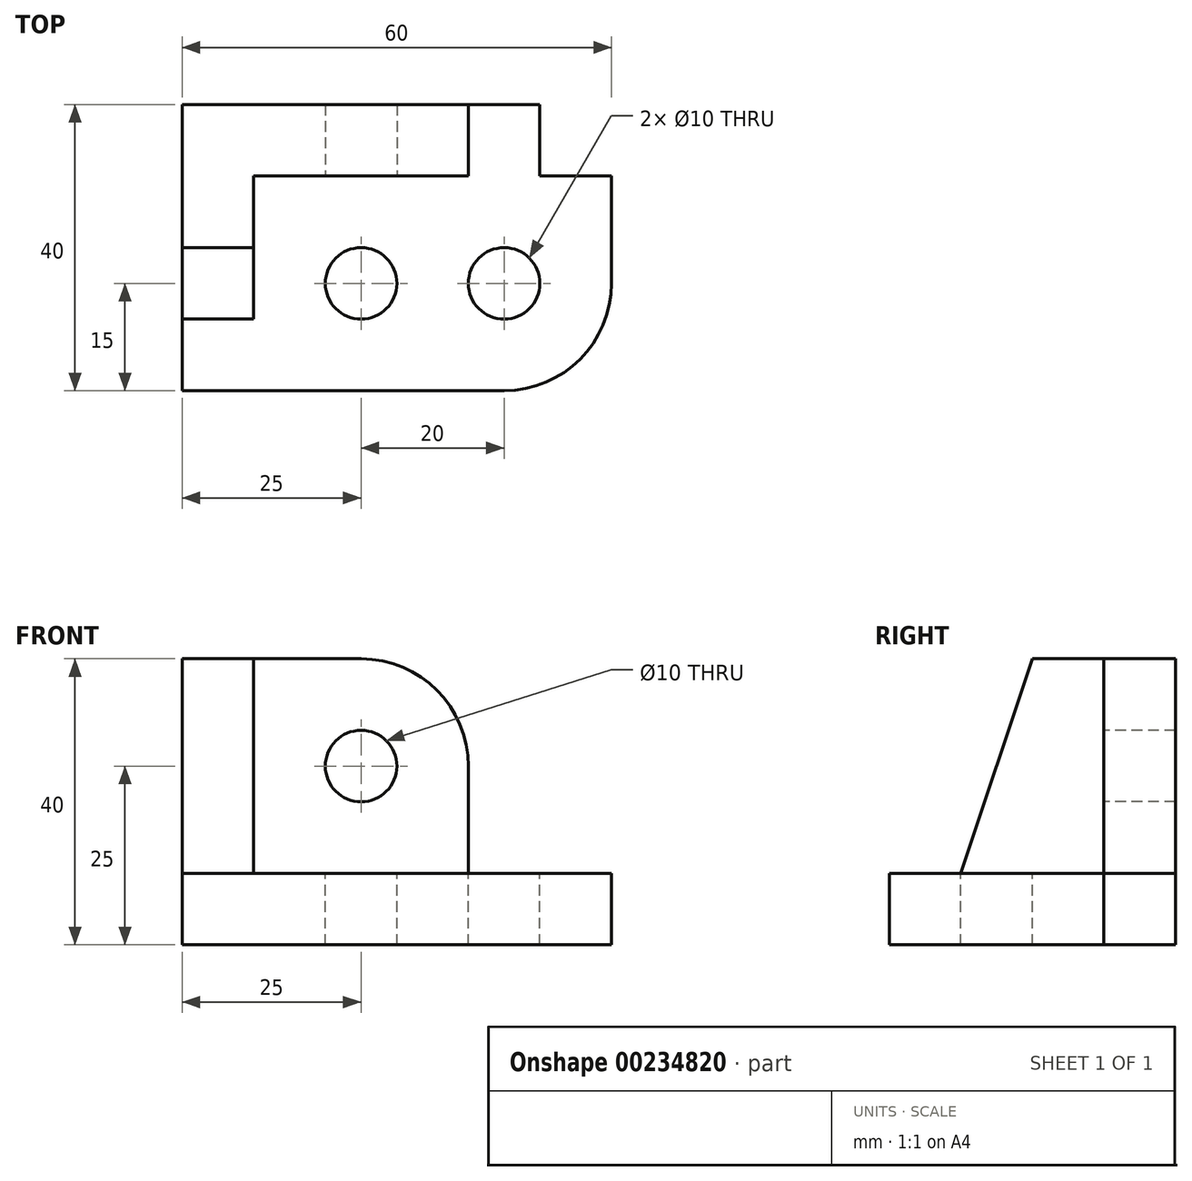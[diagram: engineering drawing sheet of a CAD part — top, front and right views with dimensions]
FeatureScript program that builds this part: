
annotation { "Feature Type Name" : "Feature", "Feature Type Description" : "" }
export const myFeature = defineFeature(function(context is Context, id is Id, definition is map)
    precondition{}
    {
        {
            var Q0;
            Q0=qCreatedBy(makeId("Top.planeOp"),FACE);
            var sketch = newSketch(context, id + "F0", { "sketchPlane" : qUnion([Q0])});
            skLineSegment(sketch, "E0.bottom", {"start": v(0, 0) * mm, "end": v(60, 0) * mm});
            skLineSegment(sketch, "E0.top", {"start": v(0, -40) * mm, "end": v(60, -40) * mm});
            skLineSegment(sketch, "E0.left", {"start": v(0, 0) * mm, "end": v(0, -40) * mm});
            skLineSegment(sketch, "E0.right", {"start": v(60, 0) * mm, "end": v(60, -40) * mm});
            skSolve(sketch);
        }
        {
            var Q0;
            Q0 = qSketchRegion(id + "F0", true);
            extrude(context, id + "F1", {"entities" : qUnion([Q0]), "depth" : 40 * mm});
        }
        {
            var Q0;
            Q0=makeQuery(id+"F1.opExtrude","CAP_FACE",FACE,{"disambiguationData":[OSD([sQuery(id+"F0.wireOp",EDGE,"E0.bottom"),sQuery(id+"F0.wireOp",EDGE,"E0.top"),sQuery(id+"F0.wireOp",EDGE,"E0.left"),sQuery(id+"F0.wireOp",EDGE,"E0.right")])],"isStart":false});
            var sketch = newSketch(context, id + "F2", { "sketchPlane" : qUnion([Q0])});
            skLineSegment(sketch, "E1.bottom", {"start": v(10, -10) * mm, "end": v(70, -10) * mm});
            skLineSegment(sketch, "E1.top", {"start": v(10, -50) * mm, "end": v(70, -50) * mm});
            skLineSegment(sketch, "E1.left", {"start": v(10, -10) * mm, "end": v(10, -50) * mm});
            skLineSegment(sketch, "E1.right", {"start": v(70, -10) * mm, "end": v(70, -50) * mm});
            skSolve(sketch);
        }
        {
            var Q0;
            Q0 = qSketchRegion(id + "F2", true);
            extrude(context, id + "F3", {"entities" : qUnion([Q0]), "operationType" : NewBodyOperationType.REMOVE, "oppositeDirection" : true, "depth" : 30 * mm});
        }
        {
            var Q0;
            Q0=makeQuery(id+"F3.boolean.opBoolean","COPY",FACE,{"derivedFrom":makeQuery(id+"F3.opExtrude","SWEPT_FACE",FACE,{"disambiguationData":[OSD([sQuery(id+"F2.wireOp",EDGE,"E1.left")])]})});
            var sketch = newSketch(context, id + "F4", { "sketchPlane" : qUnion([Q0])});
            skLineSegment(sketch, "E2", {"start": v(-20, 40) * mm, "end": v(-30, 10) * mm});
            skLineSegment(sketch, "E3", {"start": v(-30, 10) * mm, "end": v(-45, 10) * mm});
            skLineSegment(sketch, "E4", {"start": v(-45, 10) * mm, "end": v(-45, 45) * mm});
            skLineSegment(sketch, "E5", {"start": v(-45, 45) * mm, "end": v(-20, 45) * mm});
            skLineSegment(sketch, "E6", {"start": v(-20, 45) * mm, "end": v(-20, 40) * mm});
            skSolve(sketch);
        }
        {
            var Q0;
            Q0 = qSketchRegion(id + "F4", true);
            extrude(context, id + "F5", {"entities" : qUnion([Q0]), "operationType" : NewBodyOperationType.REMOVE, "endBound" : BoundingType.THROUGH_ALL, "oppositeDirection" : true, "depth" : 25 * mm});
        }
        {
            var Q0;
            Q0=makeQuery(id+"F3.boolean.opBoolean","COPY",FACE,{"derivedFrom":makeQuery(id+"F3.opExtrude","SWEPT_FACE",FACE,{"disambiguationData":[OSD([sQuery(id+"F2.wireOp",EDGE,"E1.bottom")])]})});
            var sketch = newSketch(context, id + "F6", { "sketchPlane" : qUnion([Q0])});
            skLineSegment(sketch, "E7.bottom", {"start": v(40, 45) * mm, "end": v(65, 45) * mm});
            skLineSegment(sketch, "E7.top", {"start": v(40, 10) * mm, "end": v(65, 10) * mm});
            skLineSegment(sketch, "E7.left", {"start": v(40, 45) * mm, "end": v(40, 10) * mm});
            skLineSegment(sketch, "E7.right", {"start": v(65, 45) * mm, "end": v(65, 10) * mm});
            skSolve(sketch);
        }
        {
            var Q0;
            Q0 = qSketchRegion(id + "F6", true);
            extrude(context, id + "F7", {"entities" : qUnion([Q0]), "operationType" : NewBodyOperationType.REMOVE, "endBound" : BoundingType.THROUGH_ALL, "oppositeDirection" : true, "depth" : 25 * mm});
        }
        {
            var Q0;
            Q0=makeQuery(id+"F7.boolean.opBoolean","MERGE",FACE,{"derivedFrom":[makeQuery(id+"F5.boolean.opBoolean","MERGE",FACE,{"derivedFrom":[makeQuery(id+"F3.boolean.opBoolean","COPY",FACE,{"derivedFrom":makeQuery(id+"F3.opExtrude","CAP_FACE",FACE,{"disambiguationData":[OSD([sQuery(id+"F2.wireOp",EDGE,"E1.bottom"),sQuery(id+"F2.wireOp",EDGE,"E1.top"),sQuery(id+"F2.wireOp",EDGE,"E1.left"),sQuery(id+"F2.wireOp",EDGE,"E1.right")])],"isStart":false})}),makeQuery(id+"F5.opExtrude","SWEPT_FACE",FACE,{"disambiguationData":[OSD([sQuery(id+"F4.wireOp",EDGE,"E3")])]})]}),makeQuery(id+"F7.opExtrude","SWEPT_FACE",FACE,{"disambiguationData":[OSD([sQuery(id+"F6.wireOp",EDGE,"E7.top")])]})]});
            var sketch = newSketch(context, id + "F8", { "sketchPlane" : qUnion([Q0])});
            skLineSegment(sketch, "E8.bottom", {"start": v(50, 5) * mm, "end": v(65, 5) * mm});
            skLineSegment(sketch, "E8.top", {"start": v(50, -10) * mm, "end": v(65, -10) * mm});
            skLineSegment(sketch, "E8.left", {"start": v(50, 5) * mm, "end": v(50, -10) * mm});
            skLineSegment(sketch, "E8.right", {"start": v(65, 5) * mm, "end": v(65, -10) * mm});
            skSolve(sketch);
        }
        {
            var Q0;
            Q0 = qSketchRegion(id + "F8", true);
            extrude(context, id + "F9", {"entities" : qUnion([Q0]), "operationType" : NewBodyOperationType.REMOVE, "endBound" : BoundingType.THROUGH_ALL, "oppositeDirection" : true, "depth" : 25 * mm});
        }
        {
            var Q0;
            Q0=makeQuery(id+"F7.boolean.opBoolean","MERGE",FACE,{"derivedFrom":[makeQuery(id+"F5.boolean.opBoolean","MERGE",FACE,{"derivedFrom":[makeQuery(id+"F3.boolean.opBoolean","COPY",FACE,{"derivedFrom":makeQuery(id+"F3.opExtrude","CAP_FACE",FACE,{"disambiguationData":[OSD([sQuery(id+"F2.wireOp",EDGE,"E1.bottom"),sQuery(id+"F2.wireOp",EDGE,"E1.top"),sQuery(id+"F2.wireOp",EDGE,"E1.left"),sQuery(id+"F2.wireOp",EDGE,"E1.right")])],"isStart":false})}),makeQuery(id+"F5.opExtrude","SWEPT_FACE",FACE,{"disambiguationData":[OSD([sQuery(id+"F4.wireOp",EDGE,"E3")])]})]}),makeQuery(id+"F7.opExtrude","SWEPT_FACE",FACE,{"disambiguationData":[OSD([sQuery(id+"F6.wireOp",EDGE,"E7.top")])]})]});
            var sketch = newSketch(context, id + "F10", { "sketchPlane" : qUnion([Q0])});
            skLineSegment(sketch, "E9", {"start": v(-14.31, -25) * mm, "end": v(70.55, -25) * mm, "construction": true});
            skLineSegment(sketch, "E10", {"start": v(25, -1.85) * mm, "end": v(25, -39.43) * mm, "construction": true});
            skLineSegment(sketch, "E11", {"start": v(45, -1.85) * mm, "end": v(45, -39.43) * mm, "construction": true});
            skCircle(sketch, "E12", {"center": v(25, -25) * mm, "radius": 5 * mm});
            skCircle(sketch, "E13", {"center": v(45, -25) * mm, "radius": 5 * mm});
            skSolve(sketch);
        }
        {
            var Q0;
            Q0 = qSketchRegion(id + "F10", true);
            extrude(context, id + "F11", {"entities" : qUnion([Q0]), "operationType" : NewBodyOperationType.REMOVE, "endBound" : BoundingType.THROUGH_ALL, "oppositeDirection" : true, "depth" : 25 * mm});
        }
        {
            var Q0;
            Q0=makeQuery(id+"F3.boolean.opBoolean","COPY",FACE,{"derivedFrom":makeQuery(id+"F3.opExtrude","SWEPT_FACE",FACE,{"disambiguationData":[OSD([sQuery(id+"F2.wireOp",EDGE,"E1.bottom")])]})});
            var sketch = newSketch(context, id + "F12", { "sketchPlane" : qUnion([Q0])});
            skCircle(sketch, "E14", {"center": v(25, 25) * mm, "radius": 5 * mm});
            skSolve(sketch);
        }
        {
            var Q0;
            Q0 = qSketchRegion(id + "F12", true);
            extrude(context, id + "F13", {"entities" : qUnion([Q0]), "operationType" : NewBodyOperationType.REMOVE, "endBound" : BoundingType.THROUGH_ALL, "oppositeDirection" : true, "depth" : 25 * mm});
        }
        {
            var Q0;
            Q0=makeQuery(id+"F1.opExtrude","SWEPT_EDGE",EDGE,{"disambiguationData":[OSD([sQuery(id+"F0.wireOp",EDGE,"E0.top"),sQuery(id+"F0.wireOp",EDGE,"E0.right")])]});
            fillet(context, id + "F14", {"entities" : qUnion([Q0]), "radius" : 15 * mm, "tangentPropagation" : true, "allowEdgeOverflow" : false});
        }
        {
            var Q0;
            Q0=makeQuery(id+"F7.boolean.opBoolean","INTERSECT",EDGE,{"derivedFrom":[makeQuery(id+"F1.opExtrude","CAP_FACE",FACE,{"disambiguationData":[OSD([sQuery(id+"F0.wireOp",EDGE,"E0.bottom"),sQuery(id+"F0.wireOp",EDGE,"E0.top"),sQuery(id+"F0.wireOp",EDGE,"E0.left"),sQuery(id+"F0.wireOp",EDGE,"E0.right")])],"isStart":false}),makeQuery(id+"F7.opExtrude","SWEPT_FACE",FACE,{"disambiguationData":[OSD([sQuery(id+"F6.wireOp",EDGE,"E7.left")])]})]});
            fillet(context, id + "F15", {"entities" : qUnion([Q0]), "radius" : 15 * mm, "tangentPropagation" : true, "allowEdgeOverflow" : false});
        }
    });
